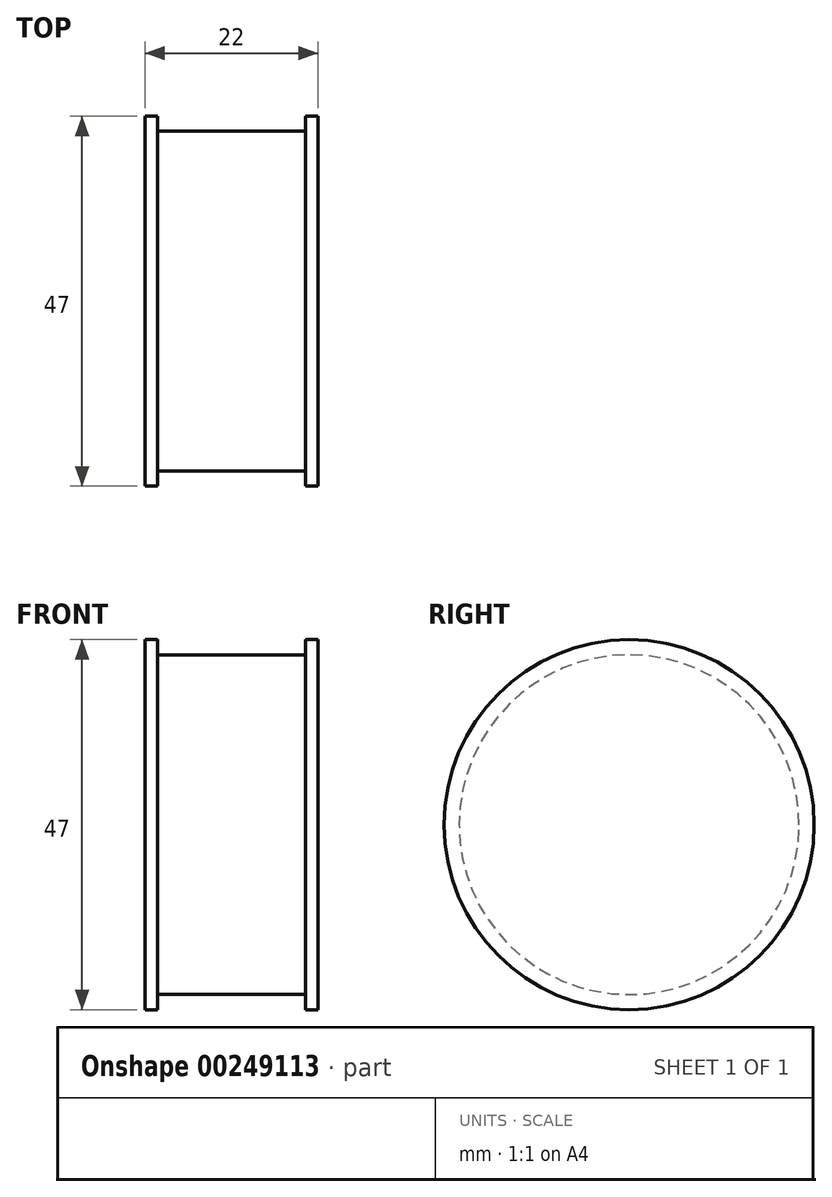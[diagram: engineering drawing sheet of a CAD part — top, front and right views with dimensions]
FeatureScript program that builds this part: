
annotation { "Feature Type Name" : "Feature", "Feature Type Description" : "" }
export const myFeature = defineFeature(function(context is Context, id is Id, definition is map)
    precondition{}
    {
        {
            var Q0;
            Q0=qCreatedBy(makeId("Front.planeOp"),FACE);
            var sketch = newSketch(context, id + "F0", { "sketchPlane" : qUnion([Q0])});
            skLineSegment(sketch, "E0", {"start": v(0, 0) * mm, "end": v(22, 0) * mm});
            skLineSegment(sketch, "E1", {"start": v(22, 0) * mm, "end": v(22, 23.5) * mm});
            skLineSegment(sketch, "E2", {"start": v(22, 23.5) * mm, "end": v(20.4, 23.5) * mm});
            skLineSegment(sketch, "E3", {"start": v(20.4, 23.5) * mm, "end": v(20.4, 21.58) * mm});
            skLineSegment(sketch, "E4", {"start": v(20.4, 21.58) * mm, "end": v(1.6, 21.58) * mm});
            skLineSegment(sketch, "E5", {"start": v(1.6, 21.58) * mm, "end": v(1.6, 23.5) * mm});
            skLineSegment(sketch, "E6", {"start": v(1.6, 23.5) * mm, "end": v(0, 23.5) * mm});
            skLineSegment(sketch, "E7", {"start": v(0, 23.5) * mm, "end": v(0, 0) * mm});
            skSolve(sketch);
        }
        {
            var Q0;
            Q0=makeQuery(id+"F0.imprint","IMPRINT",FACE,{"disambiguationData":[TD([[makeQuery(id+"F0.imprint","IMPRINT",EDGE,{"derivedFrom":sQuery(id+"F0.wireOp",EDGE,"E0")}),1.0]])]});
            var Q1;
            Q1=sQuery(id+"F0.wireOp",EDGE,"E0");
            revolve(context, id + "F1", {"entities" : qUnion([Q0]), "axis" : qUnion([Q1]), "revolveType" : RevolveType.FULL});
        }
    });
